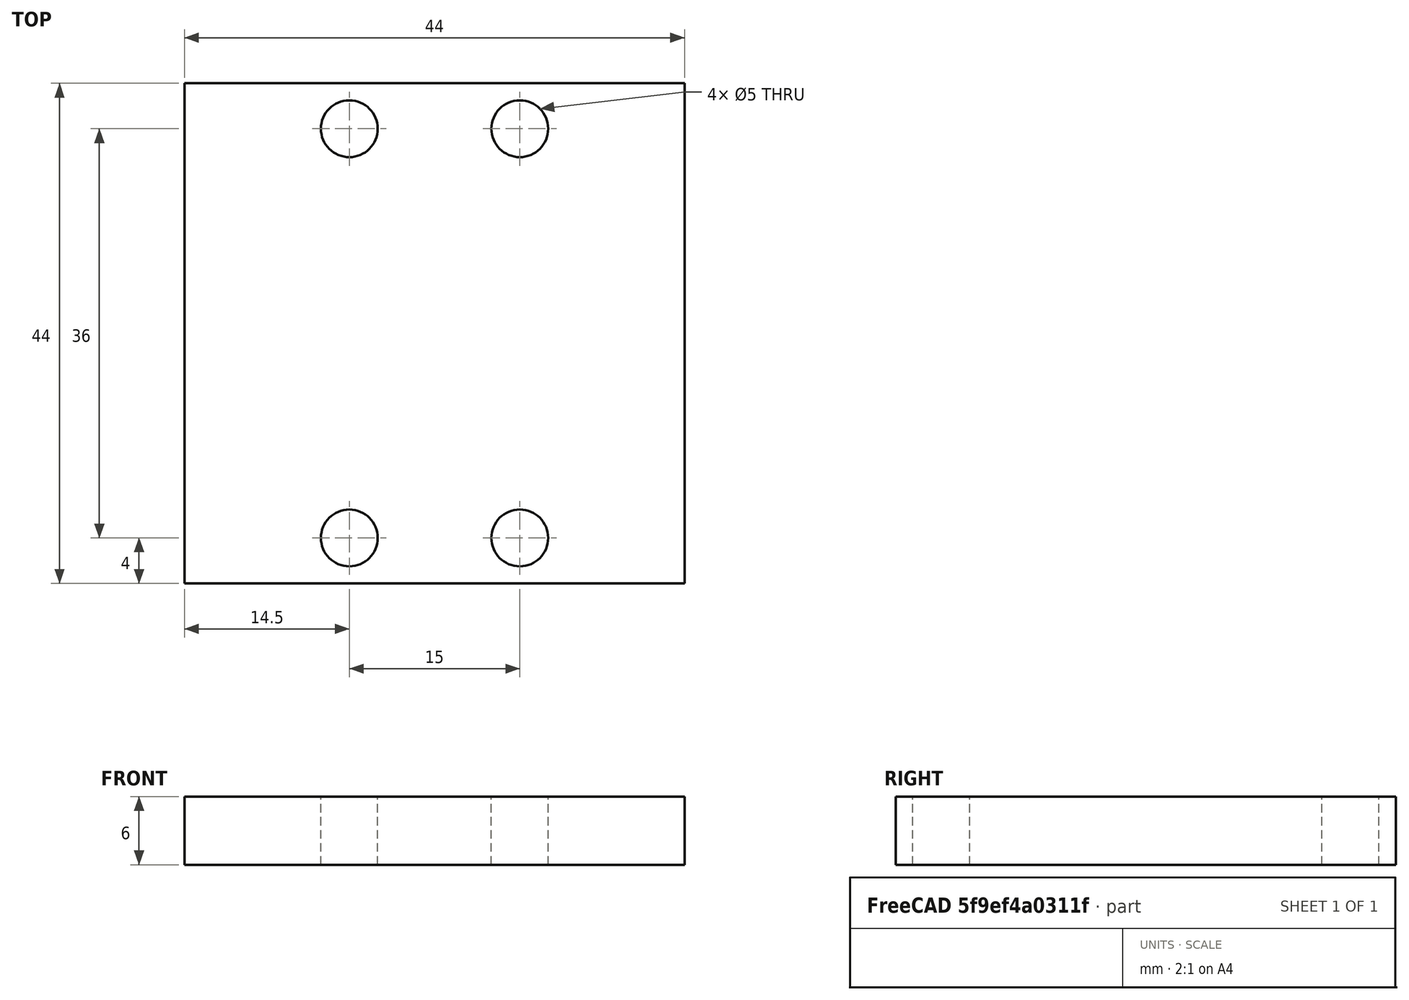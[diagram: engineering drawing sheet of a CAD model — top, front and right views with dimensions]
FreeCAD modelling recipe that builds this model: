
FCSTD DOCUMENT  (FreeCAD 0.16R)
Label: 4holes2
License: All rights reserved
LicenseURL: http://en.wikipedia.org/wiki/All_rights_reserved
objects: Part::Cylinder×4, Part::Cut×4, Part::Box×1
note: 9 computed .brp shape members not serialized (recipe doc carries the construction recipe); baked Part::Feature solids carry a one-line shape summary decoded from their .brp

FEATURE [Part::Box] Box  label="Cube"
  Height = 6
  Length = 44
  Width = 44
FEATURE [Part::Cylinder] Cylinder
  Angle = 360
  Height = 10
  Placement = pos=(14.5,4,0) rot=(0,0,1;0rad)
  Radius = 2.5
FEATURE [Part::Cylinder] Cylinder001
  Angle = 360
  Height = 10
  Placement = pos=(29.5,4,0) rot=(0,0,1;0rad)
  Radius = 2.5
FEATURE [Part::Cylinder] Cylinder002
  Angle = 360
  Height = 10
  Placement = pos=(14.5,40,0) rot=(0,0,1;0rad)
  Radius = 2.5
FEATURE [Part::Cylinder] Cylinder003
  Angle = 360
  Height = 10
  Placement = pos=(29.5,40,0) rot=(0,0,1;0rad)
  Radius = 2.5
FEATURE [Part::Cut] Cut
  Base = -> Box
  Tool = -> Cylinder
FEATURE [Part::Cut] Cut001
  Base = -> Cut
  Tool = -> Cylinder001
FEATURE [Part::Cut] Cut002
  Base = -> Cut001
  Tool = -> Cylinder002
FEATURE [Part::Cut] Cut003
  Base = -> Cut002
  Tool = -> Cylinder003
